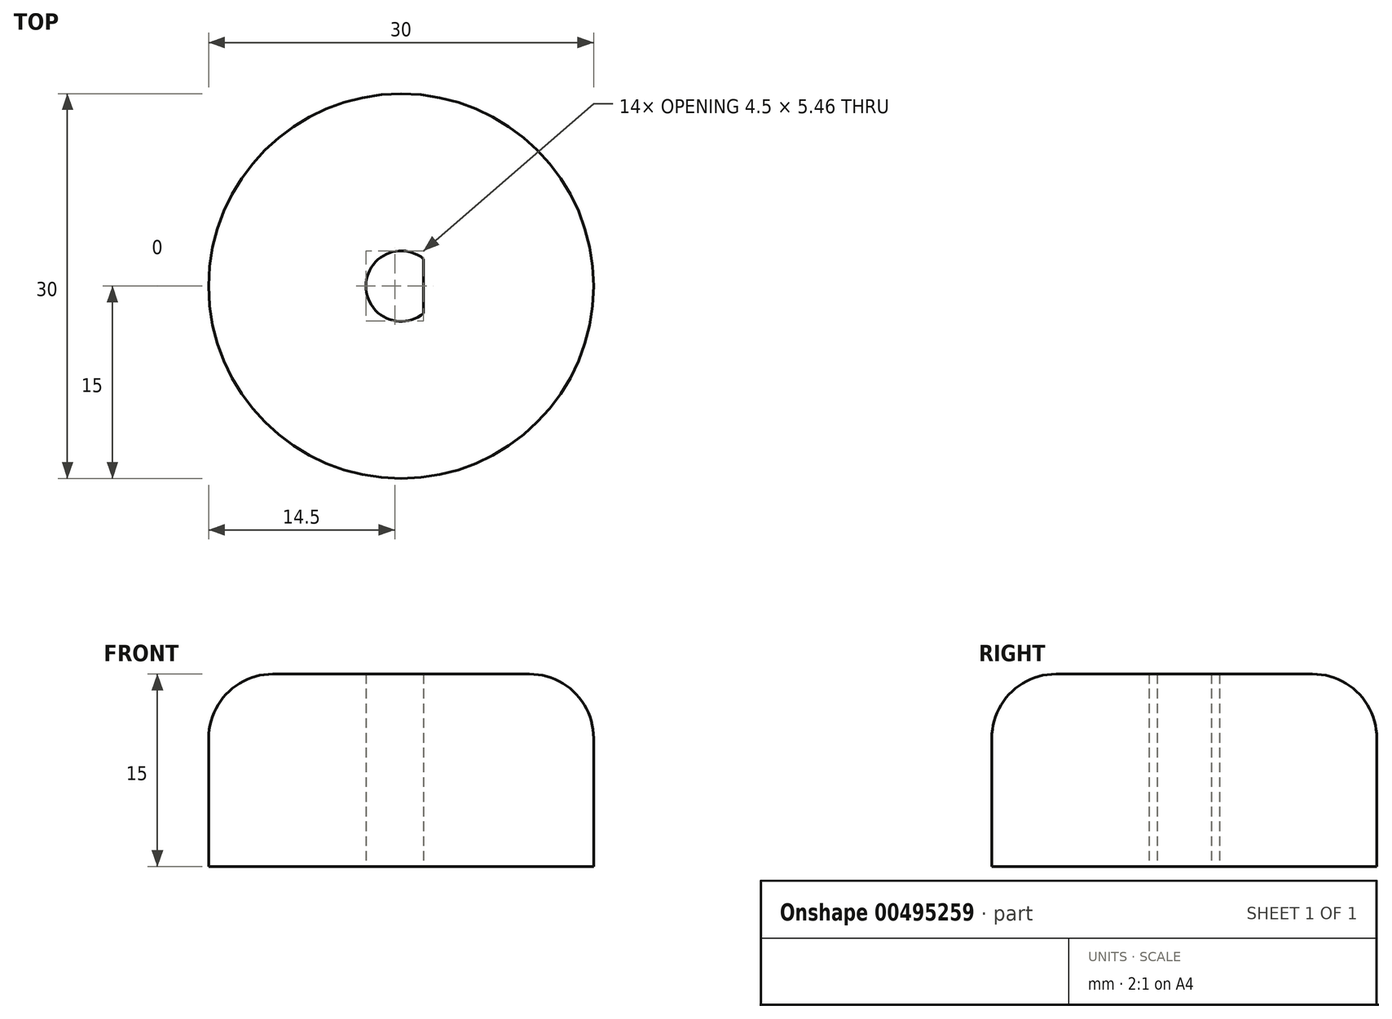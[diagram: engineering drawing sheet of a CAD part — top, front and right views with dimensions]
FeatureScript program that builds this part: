
annotation { "Feature Type Name" : "Feature", "Feature Type Description" : "" }
export const myFeature = defineFeature(function(context is Context, id is Id, definition is map)
    precondition{}
    {
        {
            var Q0;
            Q0=qCreatedBy(makeId("Top.planeOp"),FACE);
            var sketch = newSketch(context, id + "F0", { "sketchPlane" : qUnion([Q0])});
            skCircle(sketch, "E0", {"center": v(0, 0) * mm, "radius": 15 * mm});
            skSolve(sketch);
        }
        {
            var Q0;
            Q0 = qSketchRegion(id + "F0", true);
            extrude(context, id + "F1", {"entities" : qUnion([Q0]), "depth" : 15 * mm});
        }
        {
            var Q0;
            Q0=makeQuery(id+"F1.opExtrude","CAP_FACE",FACE,{"disambiguationData":[OSD([sQuery(id+"F0.wireOp",EDGE,"E0")])],"isStart":true});
            var sketch = newSketch(context, id + "F2", { "sketchPlane" : qUnion([Q0])});
            skArc(sketch, "E1", {"start": v(1.75, 2.12) * mm, "mid": v(-2.75, 0) * mm, "end": v(1.75, -2.12) * mm});
            skLineSegment(sketch, "E2", {"start": v(1.75, 2.12) * mm, "end": v(1.75, -2.12) * mm});
            skPoint(sketch, "E3.orphan", {"position": v(1.75, 3.72) * mm});
            skPoint(sketch, "E4.orphan", {"position": v(-2.75, 0) * mm});
            skPoint(sketch, "E5.end.orphan", {"position": v(1.75, 0) * mm});
            skSolve(sketch);
        }
        {
            var Q0;
            Q0 = qSketchRegion(id + "F2", true);
            extrude(context, id + "F3", {"entities" : qUnion([Q0]), "operationType" : NewBodyOperationType.REMOVE, "oppositeDirection" : true, "depth" : 25 * mm});
        }
        {
            var Q0;
            Q0=makeQuery(id+"F1.opExtrude","CAP_EDGE",EDGE,{"disambiguationData":[OSD([sQuery(id+"F0.wireOp",EDGE,"E0")])],"isStart":false});
            fillet(context, id + "F4", {"entities" : qUnion([Q0]), "radius" : 5 * mm, "tangentPropagation" : true, "allowEdgeOverflow" : false});
        }
    });
